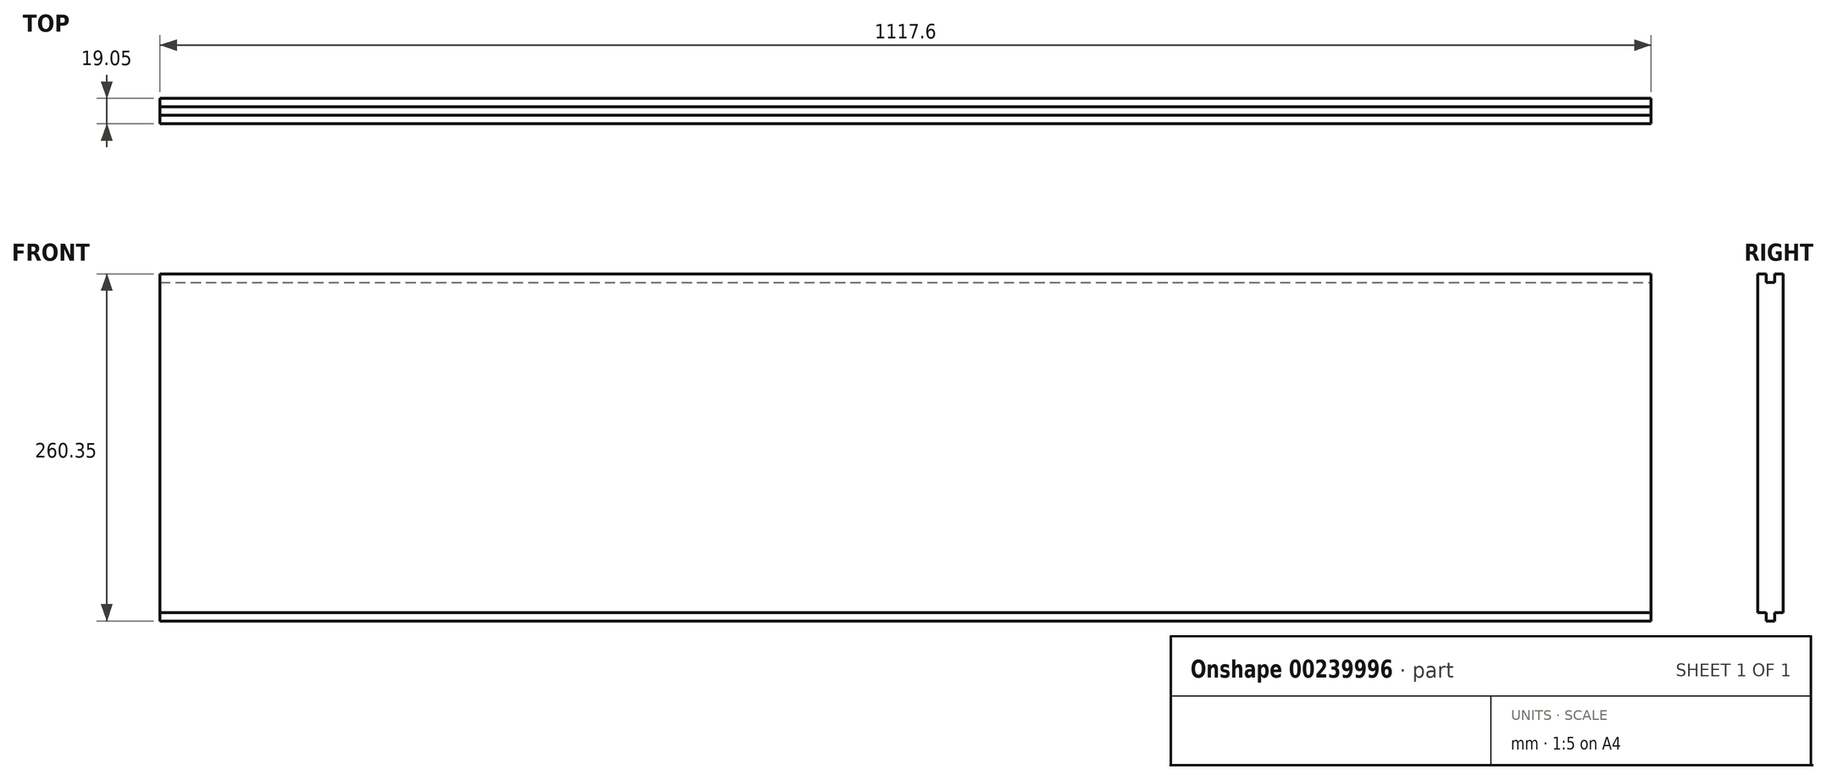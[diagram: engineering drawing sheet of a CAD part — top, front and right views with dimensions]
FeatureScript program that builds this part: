
annotation { "Feature Type Name" : "Feature", "Feature Type Description" : "" }
export const myFeature = defineFeature(function(context is Context, id is Id, definition is map)
    precondition{}
    {
        {
            var Q0;
            Q0=qCreatedBy(makeId("Front.planeOp"),FACE);
            var sketch = newSketch(context, id + "F0", { "sketchPlane" : qUnion([Q0])});
            skLineSegment(sketch, "E0.bottom", {"start": v(-599.98, -242.44) * mm, "end": v(517.62, -242.44) * mm});
            skLineSegment(sketch, "E0.top", {"start": v(-599.98, -502.8) * mm, "end": v(517.62, -502.8) * mm});
            skLineSegment(sketch, "E0.left", {"start": v(-599.98, -242.44) * mm, "end": v(-599.98, -502.8) * mm});
            skLineSegment(sketch, "E0.right", {"start": v(517.62, -242.44) * mm, "end": v(517.62, -502.8) * mm});
            skSolve(sketch);
        }
        {
            var Q0;
            Q0=makeQuery(id+"F0.imprint","IMPRINT",FACE,{"disambiguationData":[TD([[makeQuery(id+"F0.imprint","IMPRINT",EDGE,{"derivedFrom":sQuery(id+"F0.wireOp",EDGE,"E0.bottom")}),-1.0]])]});
            extrude(context, id + "F1", {"entities" : qUnion([Q0]), "depth" : 19.05 * mm, "offsetDistance" : 25.4 * mm});
        }
        {
            var Q0;
            Q0=makeQuery(id+"F1.opExtrude","SWEPT_FACE",FACE,{"disambiguationData":[OSD([sQuery(id+"F0.wireOp",EDGE,"E0.right")])]});
            var sketch = newSketch(context, id + "F2", { "sketchPlane" : qUnion([Q0])});
            skLineSegment(sketch, "E1.bottom", {"start": v(-12.7, -242.44) * mm, "end": v(-6.35, -242.44) * mm});
            skLineSegment(sketch, "E1.top", {"start": v(-12.7, -248.8) * mm, "end": v(-6.35, -248.8) * mm});
            skLineSegment(sketch, "E1.left", {"start": v(-12.7, -242.44) * mm, "end": v(-12.7, -248.8) * mm});
            skLineSegment(sketch, "E1.right", {"start": v(-6.35, -242.44) * mm, "end": v(-6.35, -248.8) * mm});
            skSolve(sketch);
        }
        {
            var Q0;
            Q0=qSketchRegion(id+"F2",true);
            extrude(context, id + "F3", {"entities" : qUnion([Q0]), "operationType" : NewBodyOperationType.REMOVE, "endBound" : BoundingType.THROUGH_ALL, "oppositeDirection" : true, "depth" : 25.4 * mm, "offsetDistance" : 25.4 * mm});
        }
        {
            var Q0;
            Q0=makeQuery(id+"F1.opExtrude","SWEPT_FACE",FACE,{"disambiguationData":[OSD([sQuery(id+"F0.wireOp",EDGE,"E0.right")])]});
            var sketch = newSketch(context, id + "F4", { "sketchPlane" : qUnion([Q0])});
            skLineSegment(sketch, "E2.bottom", {"start": v(-19.05, -496.44) * mm, "end": v(-12.7, -496.44) * mm});
            skLineSegment(sketch, "E2.top", {"start": v(-19.05, -502.8) * mm, "end": v(-12.7, -502.8) * mm});
            skLineSegment(sketch, "E2.left", {"start": v(-19.05, -496.44) * mm, "end": v(-19.05, -502.8) * mm});
            skLineSegment(sketch, "E2.right", {"start": v(-12.7, -496.44) * mm, "end": v(-12.7, -502.8) * mm});
            skLineSegment(sketch, "E3.bottom", {"start": v(-6.35, -496.44) * mm, "end": v(0, -496.44) * mm});
            skLineSegment(sketch, "E3.top", {"start": v(-6.35, -502.8) * mm, "end": v(0, -502.8) * mm});
            skLineSegment(sketch, "E3.left", {"start": v(-6.35, -496.44) * mm, "end": v(-6.35, -502.8) * mm});
            skLineSegment(sketch, "E3.right", {"start": v(0, -496.44) * mm, "end": v(0, -502.8) * mm});
            skSolve(sketch);
        }
        {
            var Q0;
            Q0=makeQuery(id+"F4.imprint","IMPRINT",FACE,{"disambiguationData":[TD([[makeQuery(id+"F4.imprint","IMPRINT",EDGE,{"derivedFrom":sQuery(id+"F4.wireOp",EDGE,"E2.bottom")}),-1.0]])]});
            var Q1;
            Q1=makeQuery(id+"F4.imprint","IMPRINT",FACE,{"disambiguationData":[TD([[makeQuery(id+"F4.imprint","IMPRINT",EDGE,{"derivedFrom":sQuery(id+"F4.wireOp",EDGE,"E3.bottom")}),-1.0]])]});
            var Q2;
            Q2=makeQuery(id+"F2.imprint","IMPRINT",FACE,{"disambiguationData":[TD([[makeQuery(id+"F2.imprint","IMPRINT",EDGE,{"derivedFrom":sQuery(id+"F2.wireOp",EDGE,"E1.bottom")}),-1.0]])]});
            extrude(context, id + "F5", {"entities" : qUnion([Q0, Q1, Q2]), "operationType" : NewBodyOperationType.REMOVE, "endBound" : BoundingType.THROUGH_ALL, "oppositeDirection" : true, "depth" : 25.4 * mm, "offsetDistance" : 25.4 * mm});
        }
    });
